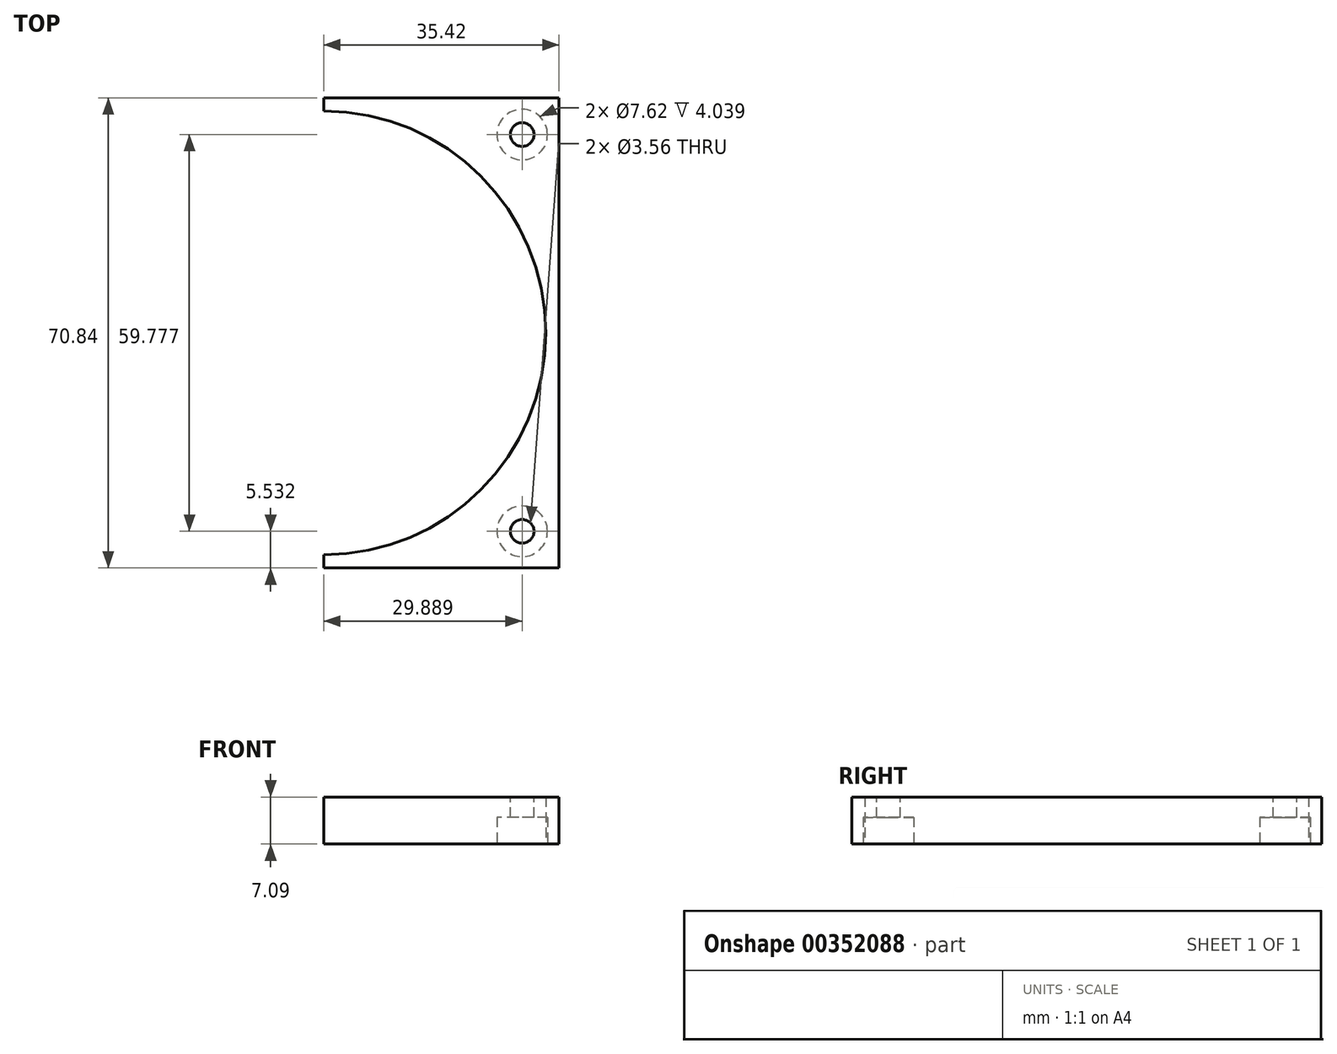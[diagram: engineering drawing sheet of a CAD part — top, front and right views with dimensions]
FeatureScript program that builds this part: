
annotation { "Feature Type Name" : "Feature", "Feature Type Description" : "" }
export const myFeature = defineFeature(function(context is Context, id is Id, definition is map)
    precondition{}
    {
        {
            var Q0;
            Q0=qCreatedBy(makeId("Top.planeOp"),FACE);
            var sketch = newSketch(context, id + "F0", { "sketchPlane" : qUnion([Q0])});
            skLineSegment(sketch, "E0.bottom", {"start": v(35.42, 0) * mm, "end": v(70.84, 0) * mm});
            skLineSegment(sketch, "E0.top", {"start": v(35.42, 70.84) * mm, "end": v(70.84, 70.84) * mm});
            skLineSegment(sketch, "E0.right", {"start": v(70.84, 0) * mm, "end": v(70.84, 70.84) * mm});
            skLineSegment(sketch, "E1", {"start": v(35.42, 0) * mm, "end": v(35.42, 1.98) * mm, "construction": true});
            skPoint(sketch, "E2", {"position": v(35.42, 35.42) * mm});
            skArc(sketch, "E3", {"start": v(35.42, 1.98) * mm, "mid": v(68.86, 35.42) * mm, "end": v(35.42, 68.86) * mm});
            skPoint(sketch, "E4", {"position": v(70.84, 0) * mm});
            skLineSegment(sketch, "E5", {"start": v(70.84, 0) * mm, "end": v(68, 2.84) * mm, "construction": true});
            skPoint(sketch, "E6", {"position": v(65.3, 5.53) * mm});
            skCircle(sketch, "E7", {"center": v(65.3, 5.53) * mm, "radius": 3.81 * mm});
            skPoint(sketch, "E8", {"position": v(65.3, 65.3) * mm});
            skCircle(sketch, "E9", {"center": v(65.3, 65.3) * mm, "radius": 3.81 * mm});
            skLineSegment(sketch, "E10", {"start": v(35.42, 0) * mm, "end": v(35.42, 1.98) * mm});
            skPoint(sketch, "E0.left.end.orphan", {"position": v(0, 70.84) * mm});
            skPoint(sketch, "E11.orphan", {"position": v(0, 0) * mm});
            skLineSegment(sketch, "E12.trimOffspring", {"start": v(65.3, 5.53) * mm, "end": v(62.61, 8.23) * mm, "construction": true});
            skLineSegment(sketch, "E13.trimOffspring", {"start": v(65.3, 65.3) * mm, "end": v(68, 68) * mm, "construction": true});
            skLineSegment(sketch, "E14.trimOffspring", {"start": v(35.42, 68.86) * mm, "end": v(35.42, 70.84) * mm, "construction": true});
            skLineSegment(sketch, "E15.trimOffspring", {"start": v(35.42, 68.86) * mm, "end": v(35.42, 70.84) * mm});
            skSolve(sketch);
        }
        {
            var Q0;
            Q0=makeQuery(id+"F0.imprint","IMPRINT",FACE,{"disambiguationData":[TD([[makeQuery(id+"F0.imprint","IMPRINT",EDGE,{"derivedFrom":sQuery(id+"F0.wireOp",EDGE,"E0.bottom")}),1.0]])]});
            extrude(context, id + "F1", {"entities" : qUnion([Q0]), "depth" : 7.1 * mm});
        }
        {
            var Q0;
            Q0=makeQuery(id+"F1.opExtrude","CAP_FACE",FACE,{"disambiguationData":[OSD([sQuery(id+"F0.wireOp",EDGE,"E0.bottom"),sQuery(id+"F0.wireOp",EDGE,"E0.top"),sQuery(id+"F0.wireOp",EDGE,"E0.right"),sQuery(id+"F0.wireOp",EDGE,"E3"),sQuery(id+"F0.wireOp",EDGE,"E7"),sQuery(id+"F0.wireOp",EDGE,"E9"),sQuery(id+"F0.wireOp",EDGE,"E10"),sQuery(id+"F0.wireOp",EDGE,"E15.trimOffspring")])],"isStart":false});
            var sketch = newSketch(context, id + "F2", { "sketchPlane" : qUnion([Q0])});
            skCircle(sketch, "E16", {"center": v(65.3, 5.53) * mm, "radius": 1.78 * mm});
            skCircle(sketch, "E17", {"center": v(65.3, 65.3) * mm, "radius": 1.78 * mm});
            skSolve(sketch);
        }
        {
            var Q0;
            Q0 = qSketchRegion(id + "F2", true);
            var Q1;
            Q1=makeQuery(id+"F2.imprint","IMPRINT",FACE,{"disambiguationData":[TD([[makeQuery(id+"F2.imprint","IMPRINT",EDGE,{"derivedFrom":sQuery(id+"F2.wireOp",EDGE,"E17")}),-1.0]])]});
            var Q2;
            Q2=makeQuery(id+"F2.imprint","IMPRINT",FACE,{"disambiguationData":[TD([[makeQuery(id+"F2.imprint","IMPRINT",EDGE,{"derivedFrom":sQuery(id+"F2.wireOp",EDGE,"E16")}),-1.0]])]});
            extrude(context, id + "F3", {"entities" : qUnion([Q0, Q1, Q2]), "operationType" : NewBodyOperationType.ADD, "oppositeDirection" : true, "depth" : 3.05 * mm});
        }
        {
            var Q0;
            Q0=makeQuery(id+"F2.imprint","IMPRINT",FACE,{"disambiguationData":[TD([[makeQuery(id+"F2.imprint","IMPRINT",EDGE,{"derivedFrom":sQuery(id+"F2.wireOp",EDGE,"E16")}),1.0]])]});
            var Q1;
            Q1=makeQuery(id+"F2.imprint","IMPRINT",FACE,{"disambiguationData":[TD([[makeQuery(id+"F2.imprint","IMPRINT",EDGE,{"derivedFrom":sQuery(id+"F2.wireOp",EDGE,"E17")}),1.0]])]});
            extrude(context, id + "F4", {"entities" : qUnion([Q0, Q1]), "operationType" : NewBodyOperationType.REMOVE, "oppositeDirection" : true, "depth" : 25.4 * mm});
        }
    });
